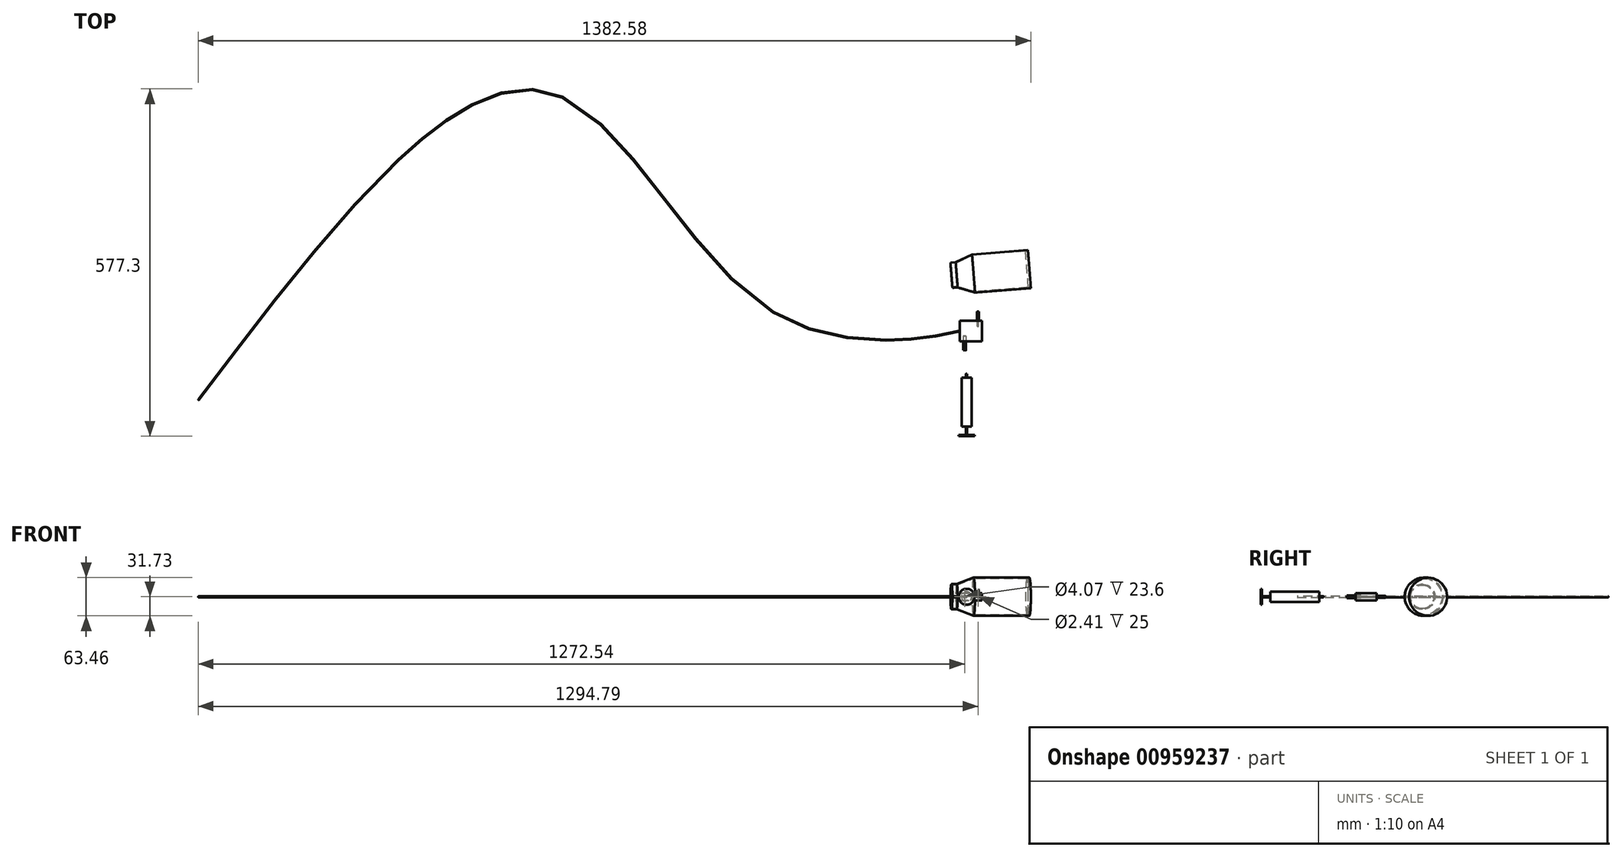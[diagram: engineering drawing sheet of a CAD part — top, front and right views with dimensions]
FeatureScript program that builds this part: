
annotation { "Feature Type Name" : "Feature", "Feature Type Description" : "" }
export const myFeature = defineFeature(function(context is Context, id is Id, definition is map)
    precondition{}
    {
        {
            var Q0;
            Q0=qCreatedBy(makeId("Top.planeOp"),FACE);
            var sketch = newSketch(context, id + "F0", { "sketchPlane" : qUnion([Q0])});
            skLineSegment(sketch, "E0", {"start": v(-62.79, 46.66) * mm, "end": v(-62.79, 12) * mm});
            skLineSegment(sketch, "E1", {"start": v(-62.79, 12) * mm, "end": v(-25.9, 12) * mm});
            skLineSegment(sketch, "E2", {"start": v(-25.9, 12) * mm, "end": v(-25.9, 46.66) * mm});
            skLineSegment(sketch, "E3", {"start": v(-25.9, 46.66) * mm, "end": v(-62.79, 46.66) * mm});
            skLineSegment(sketch, "E4", {"start": v(-31.08, 46.66) * mm, "end": v(-31.08, 61.5) * mm});
            skLineSegment(sketch, "E5", {"start": v(-31.08, 61.5) * mm, "end": v(-32.6, 61.5) * mm});
            skLineSegment(sketch, "E6", {"start": v(-32.6, 61.5) * mm, "end": v(-32.6, 46.66) * mm});
            skLineSegment(sketch, "E7", {"start": v(-54.85, 12) * mm, "end": v(-54.85, -2.75) * mm});
            skLineSegment(sketch, "E8", {"start": v(-54.85, -2.75) * mm, "end": v(-57.17, -2.75) * mm});
            skLineSegment(sketch, "E9", {"start": v(-57.17, -2.75) * mm, "end": v(-57.17, 12) * mm});
            skSolve(sketch);
        }
        {
            var Q0;
            {var subQ4=sQuery(id+"F0.wireOp",EDGE,"E0");Q0=makeQuery(id+"F0.imprint","IMPRINT",FACE,{"disambiguationData":[TD([[makeQuery(id+"F0.imprint","IMPRINT",EDGE,{"derivedFrom":subQ4}),1.0]])]});}
            extrude(context, id + "F1", {"entities" : qUnion([Q0]), "depth" : 6 * mm, "offsetDistance" : 25 * mm, "hasSecondDirection" : true, "secondDirectionOppositeDirection" : true, "secondDirectionDepth" : 6 * mm});
        }
        {
            var Q0;
            {var subQ0=sQuery(id+"F0.wireOp",EDGE,"E7");Q0=makeQuery(id+"F0.imprint","IMPRINT",FACE,{"disambiguationData":[TD([[makeQuery(id+"F0.imprint","IMPRINT",EDGE,{"derivedFrom":subQ0}),-1.0]])]});}
            var Q1;
            Q1=sQuery(id+"F0.wireOp",EDGE,"E7");
            revolve(context, id + "F2", {"operationType" : NewBodyOperationType.ADD, "surfaceOperationType" : NewSurfaceOperationType.NEW, "entities" : qUnion([Q0]), "axis" : qUnion([Q1]), "revolveType" : RevolveType.FULL});
        }
        {
            var Q0;
            {var subQ0=sQuery(id+"F0.wireOp",EDGE,"E4");Q0=makeQuery(id+"F0.imprint","IMPRINT",FACE,{"disambiguationData":[TD([[makeQuery(id+"F0.imprint","IMPRINT",EDGE,{"derivedFrom":subQ0}),1.0]])]});}
            var Q1;
            Q1=sQuery(id+"F0.wireOp",EDGE,"E6");
            revolve(context, id + "F3", {"operationType" : NewBodyOperationType.ADD, "surfaceOperationType" : NewSurfaceOperationType.NEW, "entities" : qUnion([Q0]), "axis" : qUnion([Q1]), "revolveType" : RevolveType.FULL});
        }
        {
            var Q0;
            Q0=makeQuery(id+"F2.opRevolve","SWEPT_FACE",FACE,{"disambiguationData":[OSD([sQuery(id+"F0.wireOp",EDGE,"E8")])]});
            var sketch = newSketch(context, id + "F4", { "sketchPlane" : qUnion([Q0])});
            skCircle(sketch, "E10", {"center": v(-54.85, 0) * mm, "radius": 2.04 * mm});
            skSolve(sketch);
        }
        {
            var Q0;
            Q0=makeQuery(id+"F4.imprint","IMPRINT",FACE,{"disambiguationData":[TD([[makeQuery(id+"F4.imprint","IMPRINT",EDGE,{"derivedFrom":sQuery(id+"F4.wireOp",EDGE,"E10")}),1.0]])]});
            extrude(context, id + "F5", {"entities" : qUnion([Q0]), "operationType" : NewBodyOperationType.REMOVE, "oppositeDirection" : true, "depth" : 23.6 * mm, "offsetDistance" : 25 * mm});
        }
        {
            var Q0;
            Q0=makeQuery(id+"F3.opRevolve","SWEPT_FACE",FACE,{"disambiguationData":[OSD([sQuery(id+"F0.wireOp",EDGE,"E5")])]});
            var sketch = newSketch(context, id + "F6", { "sketchPlane" : qUnion([Q0])});
            skCircle(sketch, "E11", {"center": v(32.6, 0) * mm, "radius": 1.2 * mm});
            skSolve(sketch);
        }
        {
            var Q0;
            Q0=makeQuery(id+"F6.imprint","IMPRINT",FACE,{"disambiguationData":[TD([[makeQuery(id+"F6.imprint","IMPRINT",EDGE,{"derivedFrom":sQuery(id+"F6.wireOp",EDGE,"E11")}),1.0]])]});
            extrude(context, id + "F7", {"entities" : qUnion([Q0]), "operationType" : NewBodyOperationType.REMOVE, "oppositeDirection" : true, "depth" : 25 * mm, "offsetDistance" : 25 * mm});
        }
        {
            var Q0;
            Q0=qCreatedBy(makeId("Top.planeOp"),FACE);
            var sketch = newSketch(context, id + "F8", { "sketchPlane" : qUnion([Q0])});
            skLineSegment(sketch, "E12.bottom", {"start": v(-59.84, -48.42) * mm, "end": v(-52.42, -48.42) * mm});
            skLineSegment(sketch, "E12.top", {"start": v(-59.84, -129.54) * mm, "end": v(-52.42, -129.54) * mm});
            skLineSegment(sketch, "E12.left", {"start": v(-59.84, -48.42) * mm, "end": v(-59.84, -129.54) * mm});
            skLineSegment(sketch, "E12.right", {"start": v(-52.42, -48.42) * mm, "end": v(-52.42, -129.54) * mm});
            skLineSegment(sketch, "E13", {"start": v(-52.42, -48.42) * mm, "end": v(-52.42, -41.68) * mm});
            skLineSegment(sketch, "E14", {"start": v(-52.42, -41.68) * mm, "end": v(-51.5, -41.68) * mm});
            skLineSegment(sketch, "E15", {"start": v(-51.5, -41.68) * mm, "end": v(-51.5, -48.42) * mm});
            skLineSegment(sketch, "E16", {"start": v(-51.5, -48.42) * mm, "end": v(-51.5, -129.44) * mm});
            skLineSegment(sketch, "E17", {"start": v(-51.5, -129.44) * mm, "end": v(-52.42, -129.54) * mm});
            skLineSegment(sketch, "E18", {"start": v(-52.42, -129.54) * mm, "end": v(-52.42, -143.58) * mm});
            skLineSegment(sketch, "E19", {"start": v(-52.42, -143.58) * mm, "end": v(-51.5, -143.58) * mm});
            skLineSegment(sketch, "E20", {"start": v(-51.5, -143.58) * mm, "end": v(-51.5, -129.44) * mm});
            skLineSegment(sketch, "E21", {"start": v(-52.42, -143.58) * mm, "end": v(-64.72, -143.58) * mm});
            skLineSegment(sketch, "E22", {"start": v(-64.72, -143.58) * mm, "end": v(-64.72, -145.66) * mm});
            skLineSegment(sketch, "E23", {"start": v(-64.72, -145.66) * mm, "end": v(-51.5, -145.66) * mm});
            skLineSegment(sketch, "E24", {"start": v(-51.5, -145.66) * mm, "end": v(-51.5, -143.58) * mm});
            skSolve(sketch);
        }
        {
            var Q0;
            Q0=makeQuery(id+"F8.imprint","IMPRINT",FACE,{"disambiguationData":[TD([[makeQuery(id+"F8.imprint","IMPRINT",EDGE,{"derivedFrom":sQuery(id+"F8.wireOp",EDGE,"E12.bottom")}),-1.0]])]});
            var Q1;
            Q1=makeQuery(id+"F8.imprint","IMPRINT",FACE,{"disambiguationData":[TD([[makeQuery(id+"F8.imprint","IMPRINT",EDGE,{"derivedFrom":sQuery(id+"F8.wireOp",EDGE,"E12.right")}),1.0]])]});
            var Q2;
            Q2=makeQuery(id+"F8.imprint","IMPRINT",FACE,{"disambiguationData":[TD([[makeQuery(id+"F8.imprint","IMPRINT",EDGE,{"derivedFrom":sQuery(id+"F8.wireOp",EDGE,"E17")}),1.0]])]});
            var Q3;
            Q3=makeQuery(id+"F8.imprint","IMPRINT",FACE,{"disambiguationData":[TD([[makeQuery(id+"F8.imprint","IMPRINT",EDGE,{"derivedFrom":sQuery(id+"F8.wireOp",EDGE,"E19")}),-1.0]])]});
            var Q4;
            Q4=sQuery(id+"F8.wireOp",EDGE,"E16");
            revolve(context, id + "F9", {"surfaceOperationType" : NewSurfaceOperationType.NEW, "entities" : qUnion([Q0, Q1, Q2, Q3]), "axis" : qUnion([Q4]), "revolveType" : RevolveType.FULL});
        }
        {
            var Q0;
            Q0=qCreatedBy(makeId("Top.planeOp"),FACE);
            var sketch = newSketch(context, id + "F10", { "sketchPlane" : qUnion([Q0])});
            skLineSegment(sketch, "E25", {"start": v(52.7, 132.17) * mm, "end": v(50.2, 163.8) * mm});
            skLineSegment(sketch, "E26", {"start": v(50.2, 163.8) * mm, "end": v(-42.48, 156.49) * mm});
            skLineSegment(sketch, "E27", {"start": v(-42.48, 156.49) * mm, "end": v(-69.58, 143.57) * mm});
            skLineSegment(sketch, "E28", {"start": v(-69.58, 143.57) * mm, "end": v(-78.28, 142.88) * mm});
            skLineSegment(sketch, "E29", {"start": v(-78.28, 142.88) * mm, "end": v(-78.17, 141.47) * mm});
            skLineSegment(sketch, "E30", {"start": v(-78.17, 141.47) * mm, "end": v(-69.58, 142.15) * mm});
            skLineSegment(sketch, "E31", {"start": v(-69.58, 142.15) * mm, "end": v(-42.48, 155.07) * mm});
            skLineSegment(sketch, "E32", {"start": v(-42.48, 155.07) * mm, "end": v(46.32, 162.07) * mm});
            skLineSegment(sketch, "E33", {"start": v(46.32, 162.07) * mm, "end": v(48.7, 131.85) * mm});
            skLineSegment(sketch, "E34", {"start": v(48.7, 131.85) * mm, "end": v(52.7, 132.17) * mm});
            skSolve(sketch);
        }
        {
            var Q0;
            Q0=makeQuery(id+"F10.imprint","IMPRINT",FACE,{"disambiguationData":[TD([[makeQuery(id+"F10.imprint","IMPRINT",EDGE,{"derivedFrom":sQuery(id+"F10.wireOp",EDGE,"E25")}),1.0]])]});
            var Q1;
            Q1=sQuery(id+"F10.wireOp",EDGE,"E34");
            revolve(context, id + "F11", {"surfaceOperationType" : NewSurfaceOperationType.NEW, "entities" : qUnion([Q0]), "axis" : qUnion([Q1]), "revolveType" : RevolveType.FULL});
        }
        {
            var Q0;
            Q0=qCreatedBy(makeId("Top.planeOp"),FACE);
            var sketch = newSketch(context, id + "F12", { "sketchPlane" : qUnion([Q0])});
            skFitSpline(sketch, "E35", {"points": [v(-61.63, 28.69) * mm, v(-91.67, 22.2) * mm, v(-376.76, 62.21) * mm, v(-750.08, 426.55) * mm, v(-1326.4, -85.86) * mm], "startDerivative": vector(-280.87, -72.55) * mm, "endDerivative": vector(-1644.57, -2174.23) * mm});
            skSolve(sketch);
        }
        {
            var Q0;
            Q0=makeQuery(id+"F1.opExtrude","SWEPT_FACE",FACE,{"disambiguationData":[OSD([sQuery(id+"F0.wireOp",EDGE,"E0")])]});
            var sketch = newSketch(context, id + "F13", { "sketchPlane" : qUnion([Q0])});
            skCircle(sketch, "E36", {"center": v(-29.13, 0) * mm, "radius": 0.85 * mm});
            skSolve(sketch);
        }
        {
            var Q0;
            Q0=makeQuery(id+"F13.imprint","IMPRINT",FACE,{"disambiguationData":[TD([[makeQuery(id+"F13.imprint","IMPRINT",EDGE,{"derivedFrom":sQuery(id+"F13.wireOp",EDGE,"E36")}),1.0]])]});
            var Q1;
            Q1=sQuery(id+"F12.wireOp",EDGE,"E35");
            sweep(context, id + "F14", {"operationType" : NewBodyOperationType.ADD, "profiles" : qUnion([Q0]), "path" : qUnion([Q1])});
        }
    });
